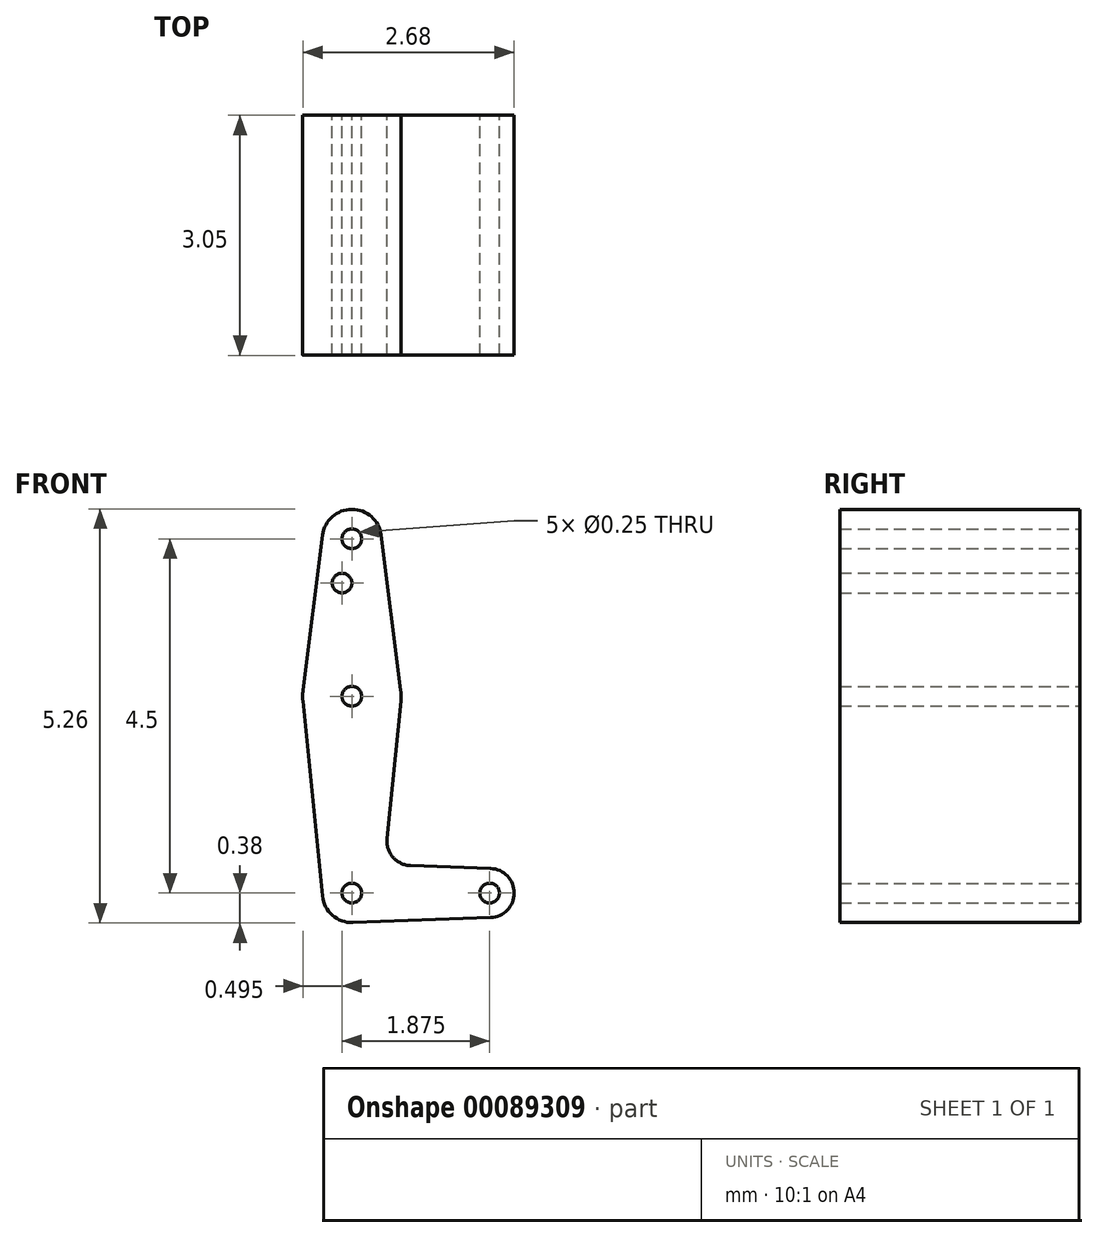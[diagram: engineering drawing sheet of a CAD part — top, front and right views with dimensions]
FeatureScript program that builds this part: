
annotation { "Feature Type Name" : "Feature", "Feature Type Description" : "" }
export const myFeature = defineFeature(function(context is Context, id is Id, definition is map)
    precondition{}
    {
        {
            var Q0;
            Q0=qCreatedBy(makeId("Front.planeOp"),FACE);
            var sketch = newSketch(context, id + "F0", { "sketchPlane" : qUnion([Q0])});
            skCircle(sketch, "E0", {"center": v(0, 0) * mm, "radius": 0.38 * mm});
            skCircle(sketch, "E1", {"center": v(0, 2.5) * mm, "radius": 0.62 * mm});
            skCircle(sketch, "E2", {"center": v(1.75, 0) * mm, "radius": 0.31 * mm});
            skCircle(sketch, "E3", {"center": v(0, 4.5) * mm, "radius": 0.38 * mm});
            skLineSegment(sketch, "E4", {"start": v(-0.37, -0.04) * mm, "end": v(-0.62, 2.44) * mm});
            skLineSegment(sketch, "E5", {"start": v(0.45, 0.7) * mm, "end": v(0.62, 2.44) * mm});
            skLineSegment(sketch, "E6", {"start": v(-0.62, 2.58) * mm, "end": v(-0.37, 4.55) * mm});
            skLineSegment(sketch, "E7", {"start": v(0.62, 2.58) * mm, "end": v(0.37, 4.55) * mm});
            skLineSegment(sketch, "E8", {"start": v(0.75, 0.35) * mm, "end": v(1.76, 0.31) * mm});
            skLineSegment(sketch, "E9", {"start": v(0.01, -0.37) * mm, "end": v(1.76, -0.31) * mm});
            skCircle(sketch, "E10", {"center": v(0, 4.5) * mm, "radius": 0.12 * mm});
            skCircle(sketch, "E11", {"center": v(0, 2.5) * mm, "radius": 0.12 * mm});
            skCircle(sketch, "E12", {"center": v(0, 0) * mm, "radius": 0.12 * mm});
            skCircle(sketch, "E13", {"center": v(1.75, 0) * mm, "radius": 0.12 * mm});
            skCircle(sketch, "E14", {"center": v(-0.12, 3.94) * mm, "radius": 0.12 * mm});
            skArc(sketch, "E15.filletArc", {"start": v(0.45, 0.7) * mm, "mid": v(0.52, 0.46) * mm, "end": v(0.75, 0.35) * mm});
            skSolve(sketch);
        }
        {
            var Q0;
            Q0 = qSketchRegion(id + "F0", true);
            extrude(context, id + "F1", {"entities" : qUnion([Q0]), "depth" : 3.05 * mm});
        }
    });
